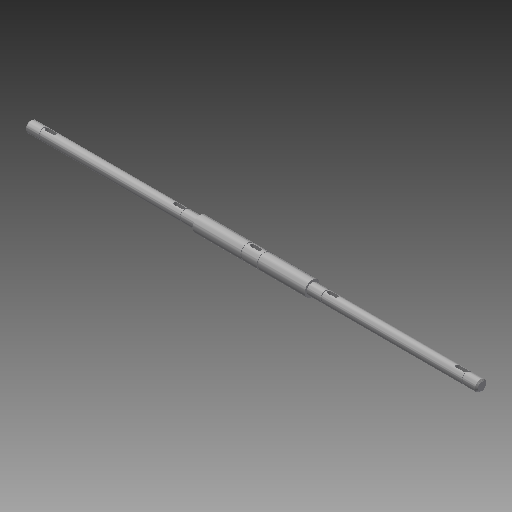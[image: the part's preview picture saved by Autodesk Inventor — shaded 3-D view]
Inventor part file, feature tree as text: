
AUTODESK INVENTOR PART (.ipt)
format: ipt  version: 2018 (Build 220112000, 112)  size: 207,872 bytes
history: native  units: mm
features: other x25, chamfer x2, revolve x1
ambient origin geometry x6: Origin, XZ Plane, XY Plane, X Axis, Y Axis, Z Axis
bodies: Solid1 (feature_tree)
feature tree (28):
  revolve  "Revolution1"  [1 undecoded]
  other  "Retaining Ring Groove6"
  other  "Retaining Ring Groove7"
  other  "Keyway8"
  other  "Keyway6"
  other  "Keyway7"
  other  "Keyway2"
  other  "Keyway3"
  other  "Retaining Ring Groove4"
  other  "Retaining Ring Groove5"
  chamfer  "Chamfer2"  Distance=4.0mm
  other  "Retaining Ring Groove3"
  other  "Retaining Ring Groove2"
  chamfer  "Chamfer1"  Distance=4.0mm
  other  "Start Plane"
  other  "Origin point"
  other  "Main Sketch"
  other  "iFeature27:2"
  other  "iFeature27:3"
  other  "iFeature27:4"
  other  "iFeature27:5"
  other  "iFeature3:2"
  other  "iFeature3:3"
  other  "iFeature3:6"
  other  "iFeature3:7"
  other  "iFeature3:8"
  other  "iFeature27:6"
  other  "iFeature27:7"
note: 1 required parameter value undecoded (feature->parameter linkage not recoverable at this tier; creation-order binding heuristic only, values carry confidence <= 0.55)
